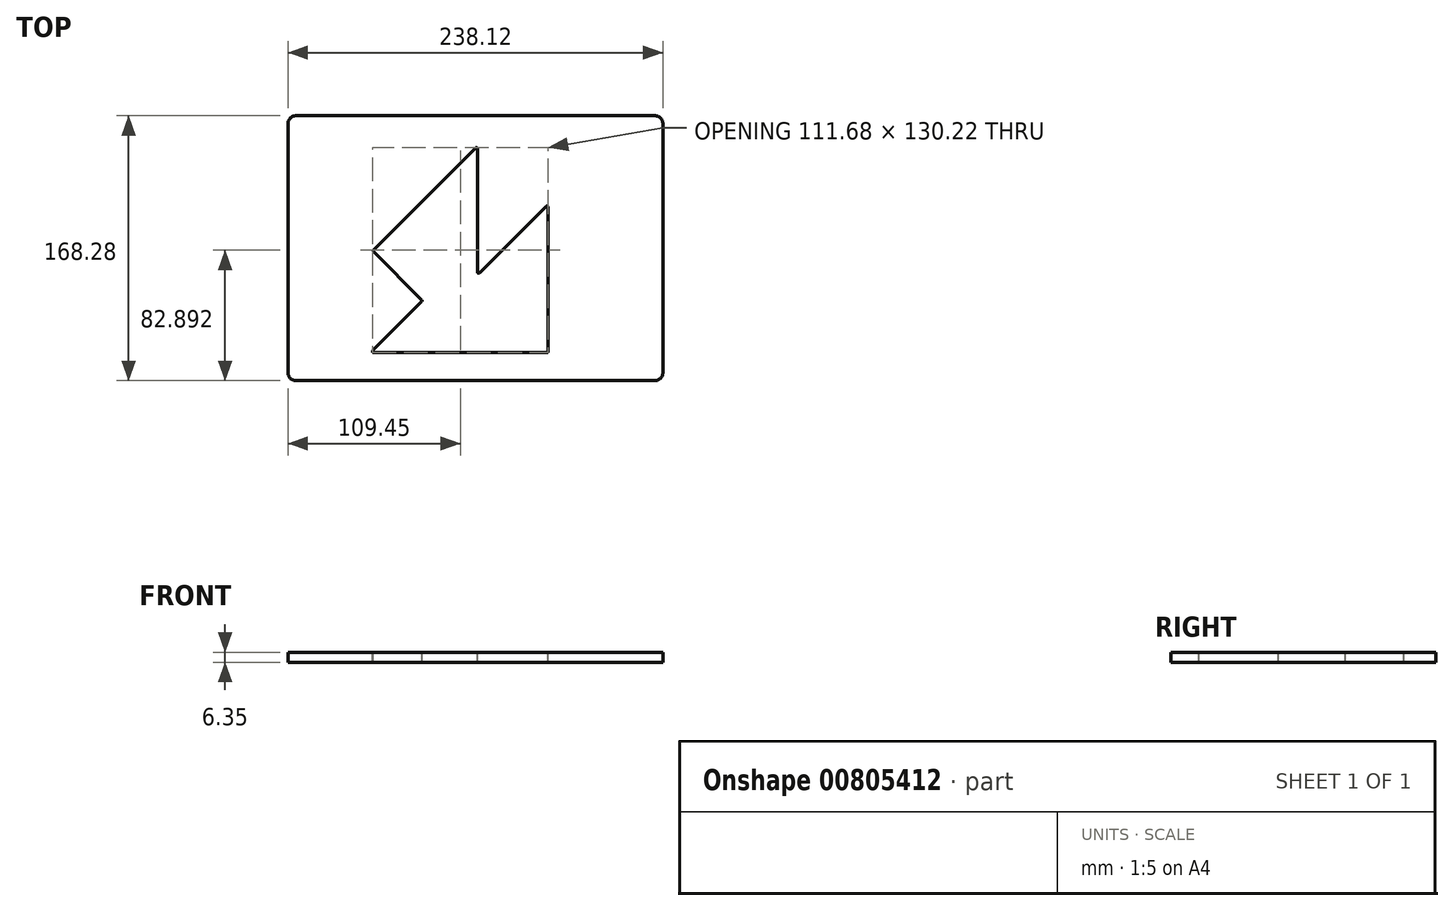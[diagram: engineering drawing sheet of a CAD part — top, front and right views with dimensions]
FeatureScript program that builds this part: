
annotation { "Feature Type Name" : "Feature", "Feature Type Description" : "" }
export const myFeature = defineFeature(function(context is Context, id is Id, definition is map)
    precondition{}
    {
        {
            var Q0;
            Q0=qCreatedBy(makeId("Top.planeOp"),FACE);
            var sketch = newSketch(context, id + "F0", { "sketchPlane" : qUnion([Q0])});
            skLineSegment(sketch, "E0.bottom", {"start": v(119.06, 84.14) * mm, "end": v(-119.06, 84.14) * mm});
            skLineSegment(sketch, "E0.top", {"start": v(119.06, -84.14) * mm, "end": v(-119.06, -84.14) * mm});
            skLineSegment(sketch, "E0.left", {"start": v(119.06, 84.14) * mm, "end": v(119.06, -84.14) * mm});
            skLineSegment(sketch, "E0.right", {"start": v(-119.06, 84.14) * mm, "end": v(-119.06, -84.14) * mm});
            skPoint(sketch, "E0.middle", {"position": v(0, 0) * mm});
            skSolve(sketch);
        }
        {
            var Q0;
            Q0 = qSketchRegion(id + "F0", true);
            extrude(context, id + "F1", {"entities" : qUnion([Q0]), "depth" : 6.35 * mm, "offsetDistance" : 25.4 * mm});
        }
        {
            var Q0;
            Q0=makeQuery(id+"F1.opExtrude","SWEPT_EDGE",EDGE,{"disambiguationData":[OSD([sQuery(id+"F0.wireOp",EDGE,"E0.top"),sQuery(id+"F0.wireOp",EDGE,"E0.left")])]});
            var Q1;
            Q1=makeQuery(id+"F1.opExtrude","SWEPT_EDGE",EDGE,{"disambiguationData":[OSD([sQuery(id+"F0.wireOp",EDGE,"E0.top"),sQuery(id+"F0.wireOp",EDGE,"E0.right")])]});
            var Q2;
            Q2=makeQuery(id+"F1.opExtrude","SWEPT_EDGE",EDGE,{"disambiguationData":[OSD([sQuery(id+"F0.wireOp",EDGE,"E0.bottom"),sQuery(id+"F0.wireOp",EDGE,"E0.left")])]});
            var Q3;
            Q3=makeQuery(id+"F1.opExtrude","SWEPT_EDGE",EDGE,{"disambiguationData":[OSD([sQuery(id+"F0.wireOp",EDGE,"E0.bottom"),sQuery(id+"F0.wireOp",EDGE,"E0.right")])]});
            fillet(context, id + "F2", {"entities" : qUnion([Q0, Q1, Q2, Q3]), "radius" : 5.08 * mm, "tangentPropagation" : true, "allowEdgeOverflow" : false});
        }
        {
            var Q0;
            Q0=makeQuery(id+"F1.opExtrude","CAP_FACE",FACE,{"disambiguationData":[OSD([sQuery(id+"F0.wireOp",EDGE,"E0.bottom"),sQuery(id+"F0.wireOp",EDGE,"E0.top"),sQuery(id+"F0.wireOp",EDGE,"E0.left"),sQuery(id+"F0.wireOp",EDGE,"E0.right")])],"isStart":false});
            var sketch = newSketch(context, id + "F3", { "sketchPlane" : qUnion([Q0])});
            skLineSegment(sketch, "E1", {"start": v(-63.5, -65.09) * mm, "end": v(44.96, -65.09) * mm});
            skLineSegment(sketch, "E2", {"start": v(44.96, -65.09) * mm, "end": v(44.96, 24.83) * mm});
            skLineSegment(sketch, "E3", {"start": v(44.96, 24.83) * mm, "end": v(0, -20.13) * mm});
            skLineSegment(sketch, "E4", {"start": v(0, -20.13) * mm, "end": v(0, 61.91) * mm});
            skLineSegment(sketch, "E5", {"start": v(0, 61.91) * mm, "end": v(-63.5, -1.59) * mm});
            skLineSegment(sketch, "E6", {"start": v(-63.5, -1.59) * mm, "end": v(-31.75, -33.34) * mm});
            skLineSegment(sketch, "E7", {"start": v(-31.75, -33.34) * mm, "end": v(-63.5, -65.09) * mm});
            skSolve(sketch);
        }
        {
            var Q0;
            Q0 = qSketchRegion(id + "F3", true);
            extrude(context, id + "F4", {"entities" : qUnion([Q0]), "operationType" : NewBodyOperationType.REMOVE, "oppositeDirection" : true, "depth" : 25.4 * mm, "offsetDistance" : 25.4 * mm});
        }
        {
            var Q0;
            Q0=makeQuery(id+"F1.opExtrude","CAP_FACE",FACE,{"disambiguationData":[OSD([sQuery(id+"F0.wireOp",EDGE,"E0.bottom"),sQuery(id+"F0.wireOp",EDGE,"E0.top"),sQuery(id+"F0.wireOp",EDGE,"E0.left"),sQuery(id+"F0.wireOp",EDGE,"E0.right")])],"isStart":false});
            var sketch = newSketch(context, id + "F5", { "sketchPlane" : qUnion([Q0])});
            skLineSegment(sketch, "E8.0", {"start": v(44.88, 26.55) * mm, "end": v(2.61, -15.72) * mm});
            skLineSegment(sketch, "E8.1", {"start": v(46.23, -65.57) * mm, "end": v(46.23, 26) * mm});
            skLineSegment(sketch, "E8.2", {"start": v(-0.07, 63.63) * mm, "end": v(-64.74, -1.03) * mm});
            skLineSegment(sketch, "E8.3", {"start": v(-64.74, -2.14) * mm, "end": v(-34.1, -32.78) * mm});
            skLineSegment(sketch, "E8.4", {"start": v(-34.1, -33.9) * mm, "end": v(-65.22, -65.01) * mm});
            skLineSegment(sketch, "E8.5", {"start": v(1.27, -15.16) * mm, "end": v(1.27, 63.08) * mm});
            skLineSegment(sketch, "E8.6", {"start": v(-64.67, -66.36) * mm, "end": v(45.44, -66.36) * mm});
            skPoint(sketch, "E9.visualSharp", {"position": v(1.27, 64.98) * mm});
            skArc(sketch, "E9.filletArc", {"start": v(1.27, 63.08) * mm, "mid": v(0.78, 63.8) * mm, "end": v(-0.07, 63.63) * mm});
            skPoint(sketch, "E10.visualSharp", {"position": v(46.23, 27.9) * mm});
            skArc(sketch, "E10.filletArc", {"start": v(46.23, 26) * mm, "mid": v(45.74, 26.72) * mm, "end": v(44.88, 26.55) * mm});
            skPoint(sketch, "E11.visualSharp", {"position": v(1.27, -17.06) * mm});
            skArc(sketch, "E11.filletArc", {"start": v(1.27, -15.16) * mm, "mid": v(1.76, -15.89) * mm, "end": v(2.61, -15.72) * mm});
            skPoint(sketch, "E12.visualSharp", {"position": v(46.23, -66.36) * mm});
            skArc(sketch, "E12.filletArc", {"start": v(45.44, -66.36) * mm, "mid": v(46, -66.13) * mm, "end": v(46.23, -65.57) * mm});
            skPoint(sketch, "E13.visualSharp", {"position": v(-66.57, -66.36) * mm});
            skArc(sketch, "E13.filletArc", {"start": v(-65.22, -65.01) * mm, "mid": v(-65.4, -65.87) * mm, "end": v(-64.67, -66.36) * mm});
            skPoint(sketch, "E14.visualSharp", {"position": v(-33.55, -33.34) * mm});
            skArc(sketch, "E14.filletArc", {"start": v(-34.1, -33.9) * mm, "mid": v(-33.87, -33.34) * mm, "end": v(-34.1, -32.78) * mm});
            skPoint(sketch, "E15.visualSharp", {"position": v(-65.3, -1.59) * mm});
            skArc(sketch, "E15.filletArc", {"start": v(-64.74, -1.03) * mm, "mid": v(-64.97, -1.59) * mm, "end": v(-64.74, -2.14) * mm});
            skSolve(sketch);
        }
        {
            var Q0;
            Q0 = qSketchRegion(id + "F5", true);
            extrude(context, id + "F6", {"entities" : qUnion([Q0]), "operationType" : NewBodyOperationType.REMOVE, "endBound" : BoundingType.THROUGH_ALL, "oppositeDirection" : true, "depth" : 25.4 * mm, "offsetDistance" : 25.4 * mm});
        }
    });
